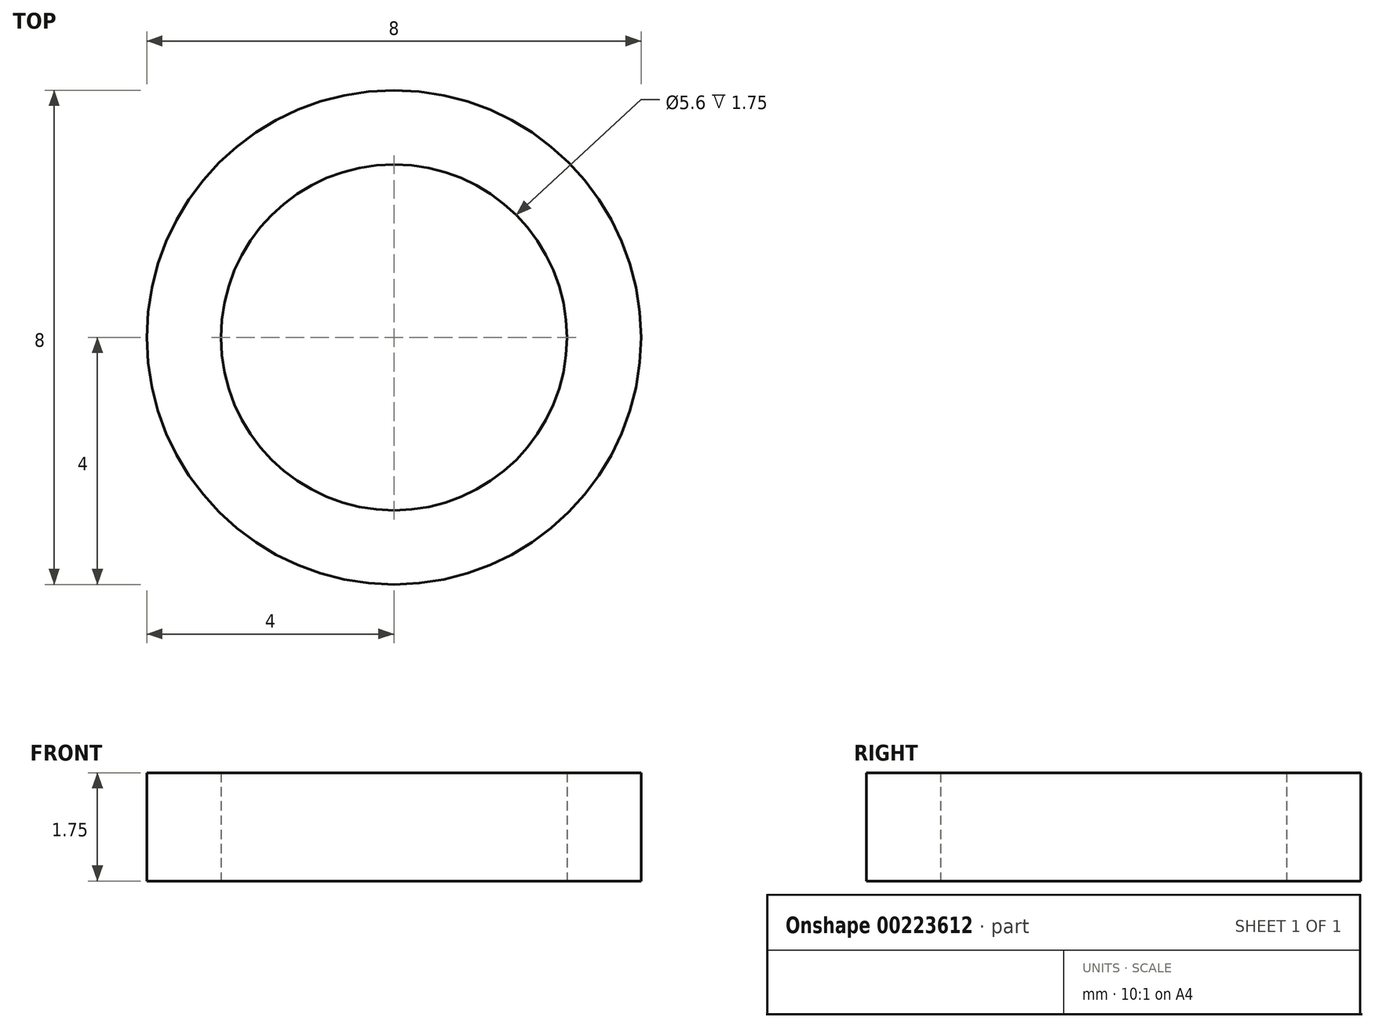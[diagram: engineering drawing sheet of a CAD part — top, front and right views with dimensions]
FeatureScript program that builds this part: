
annotation { "Feature Type Name" : "Feature", "Feature Type Description" : "" }
export const myFeature = defineFeature(function(context is Context, id is Id, definition is map)
    precondition{}
    {
        {
            var Q0;
            Q0=qCreatedBy(makeId("Top.planeOp"),FACE);
            var sketch = newSketch(context, id + "F0", { "sketchPlane" : qUnion([Q0])});
            skCircle(sketch, "E0", {"center": v(0, 0) * mm, "radius": 4 * mm});
            skCircle(sketch, "E1", {"center": v(0, 0) * mm, "radius": 2.8 * mm});
            skSolve(sketch);
        }
        {
            var Q0;
            Q0=makeQuery(id+"F0.imprint","IMPRINT",FACE,{"disambiguationData":[TD([[makeQuery(id+"F0.imprint","IMPRINT",EDGE,{"derivedFrom":sQuery(id+"F0.wireOp",EDGE,"E0")}),1.0]])]});
            var Q1;
            Q1=makeQuery(id+"F0.imprint","IMPRINT",FACE,{"disambiguationData":[TD([[makeQuery(id+"F0.imprint","IMPRINT",EDGE,{"derivedFrom":sQuery(id+"F0.wireOp",EDGE,"E1")}),-1.0]])]});
            extrude(context, id + "F1", {"entities" : qUnion([Q0, Q1]), "depth" : 1.75 * mm});
        }
    });
